# Revit family: Domotics-DomesticRanges-GEWISS-SYSTEM_POWER-SOCKET-OUTLET_ENG_16A
name_source: partatom
category: Apparecchi elettrici
revit_build: Autodesk Revit 2016 (Build: 20161004_0715(x64)
units: mm (PartAtom-declared; Revit-internal decimal feet)

## family parameters
Condiviso = Sì
Host = Superficie
Mantenere orientamento annotazione = Sì
Punto di calcolo locali = Sì
Quota connettore circolare = Usa diametro
Taglio con vuoti quando caricato = Sì
Tipo di parte = Normale

## types (2) — shared parameters
Carico apparente = 0 VA
Catalogue = DOMOTICS
Catalogue Range = SYSTEM - DOMESTIC RANGE
Description. = UK
Description: = 2P+E - 16A
Electrocod = 0131
For plug pins = Ã˜ 7 mm
IDF = de0dd1e3-30dd-4874-af10-f9f1e9b1eea3
IDT = 214929c2-afb4-4b82-b04f-9604f54146b0
Immagine tipo = GW21209.jpg
N. poli = 1
No. SYSTEM modules = 2
Produttore = GEWISS S.p.A.
Prospetto di default = 1219 mm
SEO = Socket outlet
Standard = UK
Standard: = UK
TIPO_ = System Prese Eng 16A_GENERICO : GW21209 Presa 2P+T 16A British standard nero
TXT ELETTRICO = 16
Technical sheet = https://www.gewiss.com
URL = https://www.gewiss.com
Version file RFA = 19.4
Volt = 230 V
Voltage = 250 V ac
Voltage: = 250 V ac

## per-type parameters (varying)
| type | Colour | Descrizione | EAN code | Modello |
| GW20209 - 16A 2P+E british std socket outlet white | White | 16A 2P+E BRITISH STD SOCKET OUTLET SY/WT | 8011564000612 | GW20209 |
| GW21209 - 16A 2P+E british std socket outlet black | Black | 16A 2P+E BRITISH STD SOCKET OUTLET SY/BK | 8011564128514 | GW21209 |

## geometry (parser evidence)
native form markers: Sweep x2
no freeform markers — native parametric forms only
